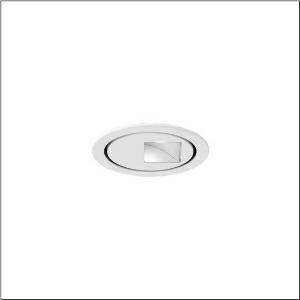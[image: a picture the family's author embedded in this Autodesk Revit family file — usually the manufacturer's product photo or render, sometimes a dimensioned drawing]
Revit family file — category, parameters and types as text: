
# Revit family: lunis_11_micro_round_51dj11b71wn21
name_source: partatom
category: Lighting Fixtures
units: mm (PartAtom-declared; Revit-internal decimal feet)

## family parameters
Cut with Voids When Loaded = No
Host = Face
Light Source = No
Part Type = Normal
Room Calculation Point = No
Round Connector Dimension = Use Diameter
Shared = No

## types (1)
- Lunis 11 micro round (1 x LED 4000K / CRI = 90 (unbekannt), 1210 lm, 4000K)
    Apparent Load = 20 VA
    CIE Flux Codes = 42 75 96 100 100
    Color Rendering = 90
    Color Temperature = 4000K
    Default Elevation = 1800 mm
    Description = Lunis 11 micro round, downlight, light control with wallwasher, of highly reflective aluminium, highly specular, light emission: direct distribution, LED rated luminous flux: 1.210lm, light colour: 940, with terminal, 3-pole, mains connection: 220..230V, AC, 50/60Hz, LED module, of aluminium, highly specular, white, diameter: 114mm, clamping range: 1..40mm, recessing ring, of plastic, traffic white (RAL 9016), protection rating (complete): IP20, insulation class (complete): insulation class II (safety insulation), certification: CE, permissible ambient temperature for indoor applications: 0..+35°C, packaging unit: 1 piece
    Height = 0 mm  [stored 0 ft]
    Lamp = 1 x LED 4000K / CRI >= 90 (unbekannt)
    Lamp Light Flux = 1210 lm
    Lamp count = 1
    Length = 114 mm
    Luminous efficacy = 61 lm/W
    Manufacturer = Siteco
    ModVariant = No
    Model = 51DJ11B71WN21
    Mounting Place = Ceiling
    Mounting Type = Recessed
    Number of Poles = 1
    OnlyDefault = Yes
    Power Factor = 1
    Product Name = Lunis 11 micro round
    Product group = downlight
    ProductGroupID = 401
    Protection Class = Protection class II
    Protection Degree = IP 20
    RLX_Detail_Level = 1
    RLX_Emergency_Light_Flux = 0 lm
    RLX_Emergency_Type = 0
    RLX_Emergency_Type_DB = No
    RlxData = <blob elided: 40945 chars, md5=8989cfea>
    Socket = socket
    Standby Power = 0 W
    System Light Flux = 1210 lm
    System Power = 20 W
    Type Comments = Product without accessories
    Type Image = l_1004773.jpg
    URL = http://relux.com
    VarID = ---
    Voltage = 0 V
    Weight = 0.00 kg
    Width = 114 mm

note: [stored X ft] marks values corroborated as IEEE doubles in the binary element streams (Revit-internal decimal feet)

## geometry (parser evidence)
native form markers: Blend x4, Sweep x9
no freeform markers — native parametric forms only
